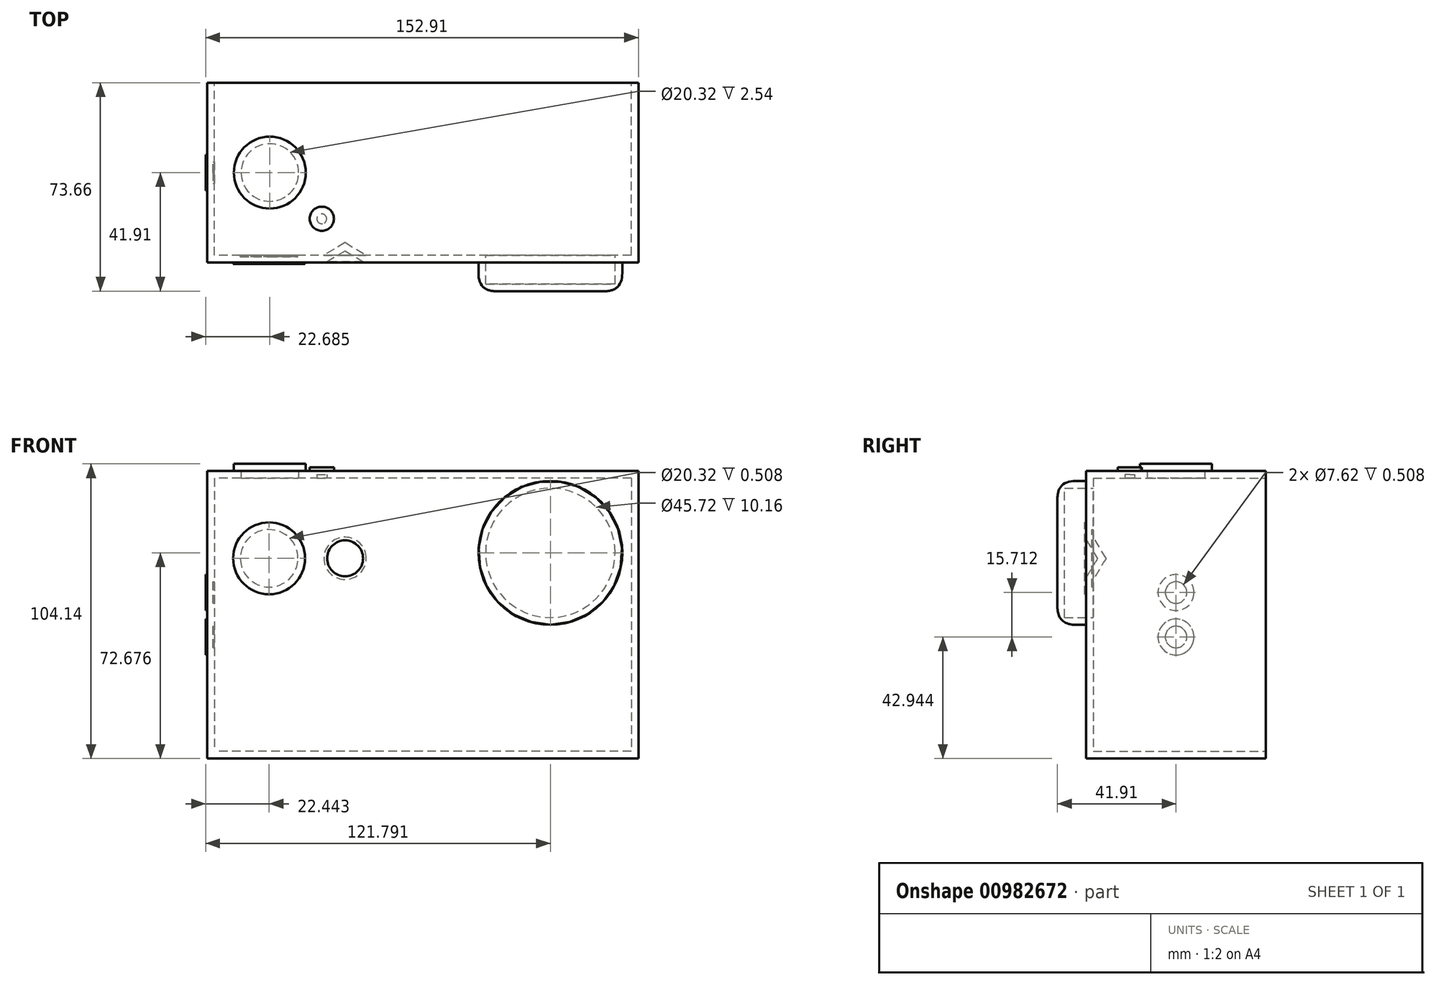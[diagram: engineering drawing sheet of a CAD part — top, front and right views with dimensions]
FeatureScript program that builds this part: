
annotation { "Feature Type Name" : "Feature", "Feature Type Description" : "" }
export const myFeature = defineFeature(function(context is Context, id is Id, definition is map)
    precondition{}
    {
        {
            var Q0;
            Q0=qCreatedBy(makeId("Front.planeOp"),FACE);
            var sketch = newSketch(context, id + "F0", { "sketchPlane" : qUnion([Q0])});
            skLineSegment(sketch, "E0.bottom", {"start": v(76.2, 50.8) * mm, "end": v(-76.2, 50.8) * mm});
            skLineSegment(sketch, "E0.top", {"start": v(76.2, -50.8) * mm, "end": v(-76.2, -50.8) * mm});
            skLineSegment(sketch, "E0.left", {"start": v(76.2, 50.8) * mm, "end": v(76.2, -50.8) * mm});
            skLineSegment(sketch, "E0.right", {"start": v(-76.2, 50.8) * mm, "end": v(-76.2, -50.8) * mm});
            skPoint(sketch, "E0.middle", {"position": v(0, 0) * mm});
            skSolve(sketch);
        }
        {
            var Q0;
            Q0=makeQuery(id+"F0.imprint","IMPRINT",FACE,{"disambiguationData":[TD([[makeQuery(id+"F0.imprint","IMPRINT",EDGE,{"derivedFrom":sQuery(id+"F0.wireOp",EDGE,"E0.bottom")}),1.0]])]});
            extrude(context, id + "F1", {"entities" : qUnion([Q0]), "endBound" : BoundingType.SYMMETRIC, "depth" : 63.5 * mm, "offsetDistance" : 25.4 * mm});
        }
        {
            var Q0;
            Q0=makeQuery(id+"F1.opExtrude","CAP_FACE",FACE,{"disambiguationData":[OSD([sQuery(id+"F0.wireOp",EDGE,"E0.bottom"),sQuery(id+"F0.wireOp",EDGE,"E0.top"),sQuery(id+"F0.wireOp",EDGE,"E0.left"),sQuery(id+"F0.wireOp",EDGE,"E0.right")])],"isStart":false});
            var sketch = newSketch(context, id + "F2", { "sketchPlane" : qUnion([Q0])});
            skCircle(sketch, "E1", {"center": v(45.08, 21.88) * mm, "radius": 25.4 * mm});
            skCircle(sketch, "E2", {"center": v(45.08, 21.88) * mm, "radius": 29.21 * mm});
            skSolve(sketch);
        }
        {
            var Q0;
            Q0=makeQuery(id+"F1.opExtrude","SWEPT_FACE",FACE,{"disambiguationData":[OSD([sQuery(id+"F0.wireOp",EDGE,"E0.bottom")])]});
            var sketch = newSketch(context, id + "F3", { "sketchPlane" : qUnion([Q0])});
            skCircle(sketch, "E3", {"center": v(-54.02, 0) * mm, "radius": 12.7 * mm});
            skSolve(sketch);
        }
        {
            var Q0;
            Q0=makeQuery(id+"F3.imprint","IMPRINT",FACE,{"disambiguationData":[TD([[makeQuery(id+"F3.imprint","IMPRINT",EDGE,{"derivedFrom":sQuery(id+"F3.wireOp",EDGE,"E3")}),1.0]])]});
            extrude(context, id + "F4", {"entities" : qUnion([Q0]), "operationType" : NewBodyOperationType.ADD, "depth" : 2.54 * mm, "offsetDistance" : 25.4 * mm});
        }
        {
            var Q0;
            Q0=makeQuery(id+"F1.opExtrude","SWEPT_FACE",FACE,{"disambiguationData":[OSD([sQuery(id+"F0.wireOp",EDGE,"E0.bottom")])]});
            var sketch = newSketch(context, id + "F5", { "sketchPlane" : qUnion([Q0])});
            skCircle(sketch, "E4", {"center": v(-35.65, -16.32) * mm, "radius": 4.28 * mm});
            skSolve(sketch);
        }
        {
            var Q0;
            Q0=makeQuery(id+"F5.imprint","IMPRINT",FACE,{"disambiguationData":[TD([[makeQuery(id+"F5.imprint","IMPRINT",EDGE,{"derivedFrom":sQuery(id+"F5.wireOp",EDGE,"E4")}),1.0]])]});
            extrude(context, id + "F6", {"entities" : qUnion([Q0]), "operationType" : NewBodyOperationType.ADD, "depth" : 1.27 * mm, "offsetDistance" : 25.4 * mm});
        }
        {
            var Q0;
            Q0=makeQuery(id+"F1.opExtrude","CAP_FACE",FACE,{"disambiguationData":[OSD([sQuery(id+"F0.wireOp",EDGE,"E0.bottom"),sQuery(id+"F0.wireOp",EDGE,"E0.top"),sQuery(id+"F0.wireOp",EDGE,"E0.left"),sQuery(id+"F0.wireOp",EDGE,"E0.right")])],"isStart":false});
            var sketch = newSketch(context, id + "F7", { "sketchPlane" : qUnion([Q0])});
            skCircle(sketch, "E5", {"center": v(-54.27, 19.94) * mm, "radius": 12.7 * mm});
            skSolve(sketch);
        }
        {
            var Q0;
            Q0=makeQuery(id+"F7.imprint","IMPRINT",FACE,{"disambiguationData":[TD([[makeQuery(id+"F7.imprint","IMPRINT",EDGE,{"derivedFrom":sQuery(id+"F7.wireOp",EDGE,"E5")}),-1.0]])]});
            var sketch = newSketch(context, id + "F8", { "sketchPlane" : qUnion([Q0])});
            skCircle(sketch, "E6", {"center": v(-27.44, 19.94) * mm, "radius": 6.35 * mm});
            skSolve(sketch);
        }
        {
            var Q0;
            Q0=makeQuery(id+"F7.imprint","IMPRINT",FACE,{"disambiguationData":[TD([[makeQuery(id+"F7.imprint","IMPRINT",EDGE,{"derivedFrom":sQuery(id+"F7.wireOp",EDGE,"E5")}),1.0]])]});
            extrude(context, id + "F9", {"entities" : qUnion([Q0]), "operationType" : NewBodyOperationType.ADD, "depth" : 0.5 * mm, "offsetDistance" : 25.4 * mm});
        }
        {
            var Q0;
            Q0=sQuery(id+"F8.wireOp",VERTEX,"E6.center");
            var Q1;
            Q1=makeQuery(id+"F1.opExtrude","SWEPT_BODY",BODY,{"disambiguationData":[OSD([sQuery(id+"F0.wireOp",EDGE,"E0.bottom"),sQuery(id+"F0.wireOp",EDGE,"E0.top"),sQuery(id+"F0.wireOp",EDGE,"E0.left"),sQuery(id+"F0.wireOp",EDGE,"E0.right")])]});
            hole(context, id + "F10", {"style" : HoleStyle.SIMPLE, "endStyle" : HoleEndStyle.BLIND, "holeDiameter" : 12.7 * mm, "majorDiameter" : 6.35 * mm, "holeDepth" : 0.25 * mm, "isTappedThrough" : true, "tappedDepth" : 12.7 * mm, "tapClearance" : 3, "locations" : qUnion([Q0]), "scope" : qUnion([Q1])});
        }
        {
            var Q0;
            Q0=makeQuery(id+"F2.imprint","IMPRINT",FACE,{"disambiguationData":[TD([[makeQuery(id+"F2.imprint","IMPRINT",EDGE,{"derivedFrom":sQuery(id+"F2.wireOp",EDGE,"E1")}),1.0]])]});
            extrude(context, id + "F11", {"entities" : qUnion([Q0]), "operationType" : NewBodyOperationType.ADD, "depth" : 10.16 * mm, "offsetDistance" : 25.4 * mm});
        }
        {
            var Q0;
            Q0=makeQuery(id+"F1.opExtrude","SWEPT_FACE",FACE,{"disambiguationData":[OSD([sQuery(id+"F0.wireOp",EDGE,"E0.right")])]});
            var sketch = newSketch(context, id + "F12", { "sketchPlane" : qUnion([Q0])});
            skCircle(sketch, "E7", {"center": v(0, 7.86) * mm, "radius": 6.35 * mm});
            skCircle(sketch, "E8", {"center": v(0, -7.86) * mm, "radius": 6.35 * mm});
            skSolve(sketch);
        }
        {
            var Q0;
            Q0=makeQuery(id+"F12.imprint","IMPRINT",FACE,{"disambiguationData":[TD([[makeQuery(id+"F12.imprint","IMPRINT",EDGE,{"derivedFrom":sQuery(id+"F12.wireOp",EDGE,"E7")}),1.0]])]});
            var Q1;
            Q1=makeQuery(id+"F12.imprint","IMPRINT",FACE,{"disambiguationData":[TD([[makeQuery(id+"F12.imprint","IMPRINT",EDGE,{"derivedFrom":sQuery(id+"F12.wireOp",EDGE,"E8")}),1.0]])]});
            extrude(context, id + "F13", {"entities" : qUnion([Q0, Q1]), "operationType" : NewBodyOperationType.ADD, "depth" : 0.5 * mm, "offsetDistance" : 25.4 * mm});
        }
        {
            var Q0;
            Q0=makeQuery(id+"F1.opExtrude","CAP_FACE",FACE,{"disambiguationData":[OSD([sQuery(id+"F0.wireOp",EDGE,"E0.bottom"),sQuery(id+"F0.wireOp",EDGE,"E0.top"),sQuery(id+"F0.wireOp",EDGE,"E0.left"),sQuery(id+"F0.wireOp",EDGE,"E0.right")])],"isStart":true});
            shell(context, id + "F14", {"entities" : qUnion([Q0]), "thickness" : 2.54 * mm});
        }
        {
            var Q0;
            Q0=makeQuery(id+"F11.opExtrude","CAP_EDGE",EDGE,{"disambiguationData":[OSD([sQuery(id+"F2.wireOp",EDGE,"E1")])],"isStart":false});
            fillet(context, id + "F15", {"entities" : qUnion([Q0]), "radius" : 6.35 * mm, "tangentPropagation" : true, "rho" : 0.5, "crossSection" : FilletCrossSection.CONIC, "allowEdgeOverflow" : false});
        }
    });
